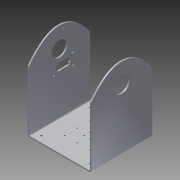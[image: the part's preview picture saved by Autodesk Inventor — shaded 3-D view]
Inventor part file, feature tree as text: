
AUTODESK INVENTOR PART (.ipt)
format: ipt  version: 2015 (Build 190159000, 159)  size: 509,952 bytes
history: native  units: in
note: dims shown in document units (in); Inventor stores cm internally (conversion verified against a paired STEP export)
features: sketch x7, other x6, sheet_metal_op x4, hole x3, chamfer x1, extrude x1, projected_geometry x1
ambient origin geometry x8: Origin, YZ Plane, XZ Plane, XY Plane, X Axis, Y Axis, Z Axis, Center Point
bodies: Body1 (feature_tree)
feature tree (23):
  sheet_metal_op  "Face2"
  sheet_metal_op  "Flange2"
  chamfer  "Corner Round1"
  hole  "Hole1"  [1 undecoded]
  sketch  "Sketch8"  dims[d193=0.0703in]
  hole  "Hole2"  [1 undecoded]
  hole  "Hole3"  [1 undecoded]
  extrude  "Extrusion1"  Depth=0.0703in
  other  "A-Side Definition"
  sketch  "Sketch3"  dims[d174=0.125in d185=6.25in]
  other  "Plate3"
  sketch  "Sketch4"  dims[d186=6.0in d187=0.0703in]
  other  "Plate4"
  sheet_metal_op  "Bend2"
  sheet_metal_op  "Corner2"
  sketch  "Sketch5"  dims[d188=0.0703in d189=0.0703in]
  sketch  "Sketch6"  dims[d190=0.0703in d191=0.0703in]
  sketch  "Sketch7"  dims[d192=0.0703in]
  sketch  "Sketch9"  dims[d194=0.072in d195=0.072in d196=0.0703in d197=0.0703in d198=0.0703in d199=0.072in d200=0.072in d201=0.0703in d202=0.0703in d203=0.072in d204=0.0703in d205=1.97in d206=1.97in d207=0.25in d208=0.25in d209=0.0703in d210=0.072in d211=0.0703in d212=0.0703in d213=0.072in d214=0.072in d215=0.0703in d216=0.0703in d217=0.0703in d218=0.072in d219=0.0703in d220=0.0703in d221=0.0703in d222=0.0703in d223=0.0703in d224=0.0703in d225=2.9297in d226=1.375in d227=3.0in d228=3.0in d229=2.9297in d230=1.875in d231=3.0in d232=3.0in d233=1.6922in d234=1.8876in d235=1.7626in d236=1.7626in d237=4.1671in d238=1.8876in d239=4.2374in d240=4.2374in d241=2.0458in d242=2.2411in d243=2.1161in d244=2.1161in d245=3.8136in d246=2.2411in d247=3.8839in d248=3.8839in d249=2.928in d250=2.375in d251=3.0in d252=3.0in d253=2.3994in d254=2.5947in d255=2.4697in d256=2.4697in d257=3.46in d258=2.5947in d259=3.5303in d260=3.5303in d261=2.9297in d262=2.74in d263=3.0in d264=3.0in d265=2.6558in d266=2.8528in d267=2.7278in d268=2.7278in d269=3.2002in d270=2.8528in d271=3.2722in d272=3.2722in d273=1.03in d274=3.125in d275=1.1797in d276=3.125in d277=1.25in d278=1.25in d279=1.6797in d280=3.125in d281=1.75in d282=1.75in d283=2.178in d284=3.125in d285=2.25in d286=2.25in d287=2.5447in d288=3.125in d289=2.615in d290=2.615in d291=2.75in d292=3.125in d293=3.0in d294=3.0in d295=3.3147in d296=3.125in d297=3.385in d298=3.385in d299=3.678in d300=3.125in d301=3.75in d302=3.75in d303=4.1797in d304=3.125in d305=4.25in d306=4.25in d307=4.6797in d308=3.125in d309=4.75in d310=4.75in d311=2.6558in d312=3.3972in d313=2.7278in d314=2.7278in d315=3.2002in d316=3.3972in d317=3.2722in d318=3.2722in d319=2.9297in d320=3.51in d321=3.0in d322=3.0in d323=2.3994in d324=3.6553in d325=2.4697in d326=2.4697in d327=3.46in d328=3.6553in d329=3.5303in d330=3.5303in d331=2.928in d332=3.875in d333=3.0in d334=3.0in d335=2.0458in d336=4.0089in d337=2.1161in d338=2.1161in d339=3.8136in d340=4.0089in d341=3.8839in d342=3.8839in d343=1.6922in d344=4.3624in d345=1.7626in d346=1.7626in d347=4.1671in d348=4.3624in d349=4.2374in d350=4.2374in d351=2.9297in d352=4.375in d353=3.0in d354=3.0in d355=2.9297in d356=4.875in d357=3.0in d358=3.0in d359=0.125in d360=0.125in d361=0.0625in d362=0.25in d363=0.125in d364=8.0in d365=90.0deg d366=0.125in d367=0.5in d368=0.125in d369=0.125in d370=6.0in d371=2.0in d372=1.5in d373=0.125in d374=0.0in d375=0.25in d376=2.9736in d377=2.9736in d378=0.094in d379=0.094in d380=0.094in d381=0.094in d382=0.094in d383=0.094in d384=0.094in d385=0.094in d386=6.063in d387=6.063in d388=3.0315in d389=3.0315in d390=2.383in d391=2.383in d392=2.383in d393=2.383in d394=2.383in d395=2.383in d396=2.383in d397=2.383in d398=4.6195in d399=0.711in d400=5.477in d401=0.711in d402=5.477in d403=0.19in d404=0.75in d405=0.375in d406=0.25in d407=0.5635in d408=0.125in d409=0.8108in d410=0.732in d411=1.5in d412=0.489in d413=0.8268in d414=0.3494in d415=0.3494in d416=0.1517in d417=0.125in d418=0.0in d419=0.144in d420=0.75in d421=0.279in d422=0.25in d423=0.5635in d424=0.125in d425=0.8108in d426=0.104in d427=0.276in d428=0.279in d429=0.25in d430=0.5635in d431=0.432in d432=0.8108in d433=1.0in d434=0.0in]
  projected_geometry  "Projected Loop1"
  other  "Cut1"
  other  "Cut2"
  other  "Definition1"
note: 3 required parameter values undecoded (feature->parameter linkage not recoverable at this tier; creation-order binding heuristic only, values carry confidence <= 0.55)
